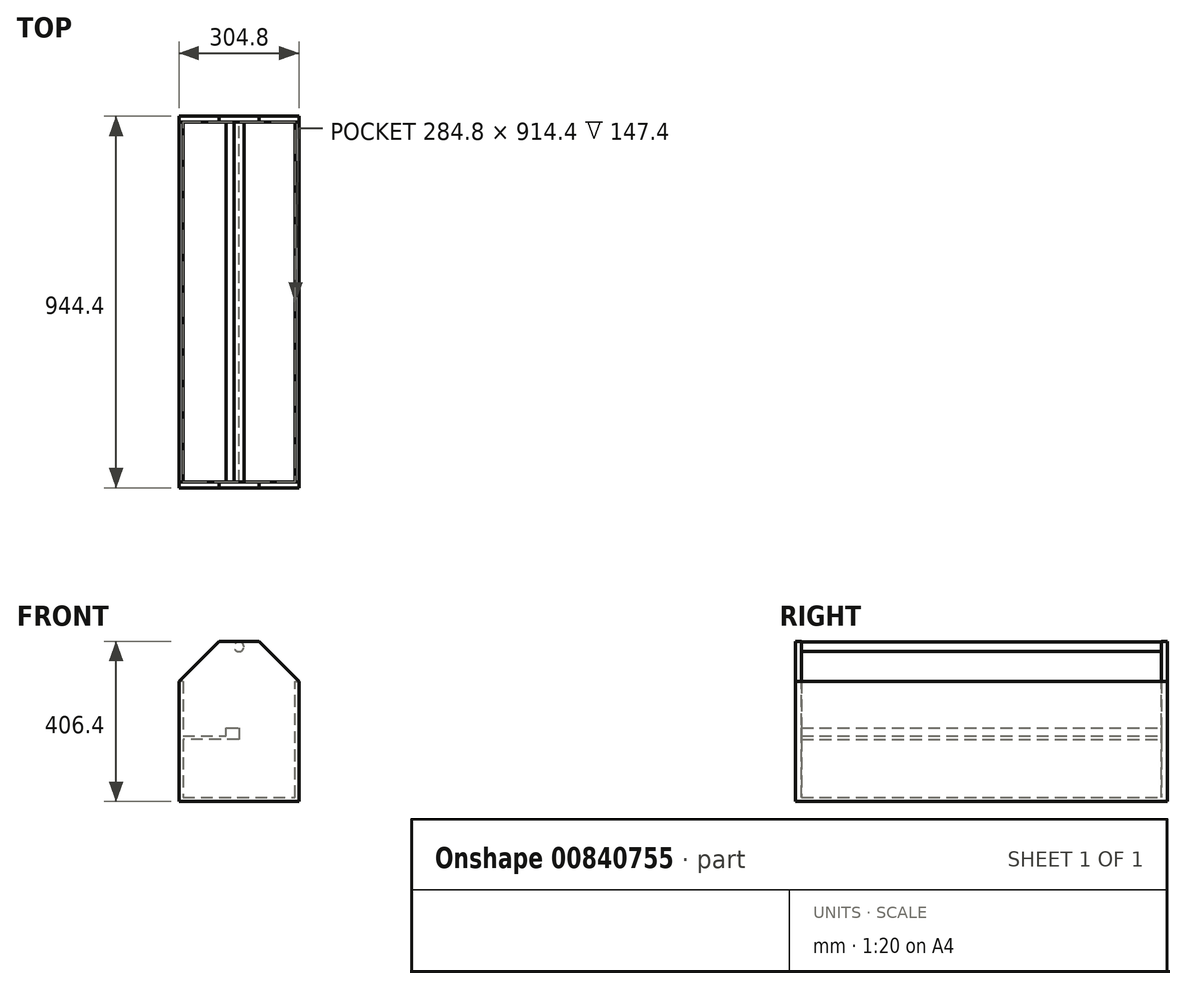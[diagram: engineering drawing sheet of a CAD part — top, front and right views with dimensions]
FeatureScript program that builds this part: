
annotation { "Feature Type Name" : "Feature", "Feature Type Description" : "" }
export const myFeature = defineFeature(function(context is Context, id is Id, definition is map)
    precondition{}
    {
        {
            var Q0;
            Q0=qCreatedBy(makeId("Front.planeOp"),FACE);
            var sketch = newSketch(context, id + "F0", { "sketchPlane" : qUnion([Q0])});
            skLineSegment(sketch, "E0", {"start": v(0, 0) * mm, "end": v(0, -304.8) * mm});
            skLineSegment(sketch, "E1", {"start": v(0, -304.8) * mm, "end": v(304.8, -304.8) * mm});
            skLineSegment(sketch, "E2", {"start": v(304.8, -304.8) * mm, "end": v(304.8, 0) * mm});
            skLineSegment(sketch, "E3", {"start": v(304.8, 0) * mm, "end": v(203.2, 101.6) * mm});
            skLineSegment(sketch, "E4", {"start": v(203.2, 101.6) * mm, "end": v(101.6, 101.6) * mm});
            skLineSegment(sketch, "E5", {"start": v(101.6, 101.6) * mm, "end": v(0, 0) * mm});
            skSolve(sketch);
        }
        {
            var Q0;
            Q0 = qSketchRegion(id + "F0", true);
            extrude(context, id + "F1", {"entities" : qUnion([Q0]), "depth" : 15 * mm, "offsetDistance" : 25 * mm});
        }
        {
            var Q0;
            Q0=makeQuery(id+"F1.opExtrude","CAP_FACE",FACE,{"disambiguationData":[OSD([sQuery(id+"F0.wireOp",EDGE,"E0"),sQuery(id+"F0.wireOp",EDGE,"E1"),sQuery(id+"F0.wireOp",EDGE,"E2"),sQuery(id+"F0.wireOp",EDGE,"E3"),sQuery(id+"F0.wireOp",EDGE,"E4"),sQuery(id+"F0.wireOp",EDGE,"E5")])],"isStart":false});
            var sketch = newSketch(context, id + "F2", { "sketchPlane" : qUnion([Q0])});
            skCircle(sketch, "E6", {"center": v(152.4, 87.99) * mm, "radius": 12.5 * mm});
            skPoint(sketch, "E6.centerSnap0", {"position": v(152.4, 101.6) * mm});
            skSolve(sketch);
        }
        {
            var Q0;
            Q0 = qSketchRegion(id + "F2", true);
            extrude(context, id + "F3", {"entities" : qUnion([Q0]), "operationType" : NewBodyOperationType.ADD, "depth" : 914.4 * mm, "offsetDistance" : 25 * mm});
        }
        {
            var Q0;
            Q0=makeQuery(id+"F1.opExtrude","CAP_FACE",FACE,{"disambiguationData":[OSD([sQuery(id+"F0.wireOp",EDGE,"E0"),sQuery(id+"F0.wireOp",EDGE,"E1"),sQuery(id+"F0.wireOp",EDGE,"E2"),sQuery(id+"F0.wireOp",EDGE,"E3"),sQuery(id+"F0.wireOp",EDGE,"E4"),sQuery(id+"F0.wireOp",EDGE,"E5")])],"isStart":false});
            var sketch = newSketch(context, id + "F4", { "sketchPlane" : qUnion([Q0])});
            skLineSegment(sketch, "E7.0", {"start": v(294.8, -294.8) * mm, "end": v(294.8, 0) * mm});
            skLineSegment(sketch, "E7.1", {"start": v(10, -294.8) * mm, "end": v(294.8, -294.8) * mm});
            skLineSegment(sketch, "E7.2", {"start": v(10, 0) * mm, "end": v(10, -294.8) * mm});
            skLineSegment(sketch, "E8", {"start": v(294.8, 0) * mm, "end": v(304.8, 0) * mm});
            skLineSegment(sketch, "E9", {"start": v(10, 0) * mm, "end": v(0, 0) * mm});
            skSolve(sketch);
        }
        {
            var Q0;
            Q0=makeQuery(id+"F4.imprint","IMPRINT",FACE,{"disambiguationData":[TD([[makeQuery(id+"F4.imprint","IMPRINT",EDGE,{"derivedFrom":sQuery(id+"F4.wireOp",EDGE,"E7.0")}),-1.0]])]});
            extrude(context, id + "F5", {"entities" : qUnion([Q0]), "operationType" : NewBodyOperationType.ADD, "depth" : 914.4 * mm, "offsetDistance" : 25 * mm});
        }
        {
            var Q0;
            Q0=makeQuery(id+"F5.opExtrude","CAP_FACE",FACE,{"disambiguationData":[OSD([sQuery(id+"F0.wireOp",EDGE,"E0"),sQuery(id+"F0.wireOp",EDGE,"E1"),sQuery(id+"F0.wireOp",EDGE,"E2"),sQuery(id+"F4.wireOp",EDGE,"E7.0"),sQuery(id+"F4.wireOp",EDGE,"E7.1"),sQuery(id+"F4.wireOp",EDGE,"E7.2"),sQuery(id+"F4.wireOp",EDGE,"E8"),sQuery(id+"F4.wireOp",EDGE,"E9")])],"isStart":false});
            var sketch = newSketch(context, id + "F6", { "sketchPlane" : qUnion([Q0])});
            skLineSegment(sketch, "E10", {"start": v(0, -304.8) * mm, "end": v(0, 0) * mm});
            skLineSegment(sketch, "E11", {"start": v(0, 0) * mm, "end": v(101.6, 101.6) * mm});
            skLineSegment(sketch, "E12", {"start": v(101.6, 101.6) * mm, "end": v(203.2, 101.6) * mm});
            skLineSegment(sketch, "E13", {"start": v(203.2, 101.6) * mm, "end": v(304.8, 0) * mm});
            skLineSegment(sketch, "E14", {"start": v(304.8, 0) * mm, "end": v(304.8, -304.8) * mm});
            skLineSegment(sketch, "E15", {"start": v(304.8, -304.8) * mm, "end": v(0, -304.8) * mm});
            skSolve(sketch);
        }
        {
            var Q0;
            Q0 = qSketchRegion(id + "F6", true);
            extrude(context, id + "F7", {"entities" : qUnion([Q0]), "operationType" : NewBodyOperationType.ADD, "depth" : 15 * mm, "offsetDistance" : 25 * mm});
        }
        {
            var Q0;
            Q0=makeQuery(id+"F1.opExtrude","CAP_FACE",FACE,{"disambiguationData":[OSD([sQuery(id+"F0.wireOp",EDGE,"E0"),sQuery(id+"F0.wireOp",EDGE,"E1"),sQuery(id+"F0.wireOp",EDGE,"E2"),sQuery(id+"F0.wireOp",EDGE,"E3"),sQuery(id+"F0.wireOp",EDGE,"E4"),sQuery(id+"F0.wireOp",EDGE,"E5")])],"isStart":false});
            var sketch = newSketch(context, id + "F8", { "sketchPlane" : qUnion([Q0])});
            skLineSegment(sketch, "E16", {"start": v(152.4, -147.4) * mm, "end": v(10, -147.4) * mm});
            skPoint(sketch, "E16.startSnap0", {"position": v(10, -147.4) * mm});
            skPoint(sketch, "E16.startSnap1", {"position": v(152.4, 101.6) * mm});
            skLineSegment(sketch, "E17", {"start": v(10, -147.4) * mm, "end": v(10, -138.6) * mm});
            skLineSegment(sketch, "E18", {"start": v(152.4, -118.6) * mm, "end": v(152.4, -147.4) * mm});
            skLineSegment(sketch, "E19", {"start": v(10, -138.6) * mm, "end": v(120, -138.6) * mm});
            skLineSegment(sketch, "E20", {"start": v(120, -138.6) * mm, "end": v(120, -118.6) * mm});
            skLineSegment(sketch, "E21", {"start": v(120, -118.6) * mm, "end": v(152.4, -118.6) * mm});
            skSolve(sketch);
        }
        {
            var Q0;
            Q0 = qSketchRegion(id + "F8", true);
            extrude(context, id + "F9", {"entities" : qUnion([Q0]), "operationType" : NewBodyOperationType.ADD, "depth" : 914.4 * mm, "offsetDistance" : 25 * mm});
        }
    });
